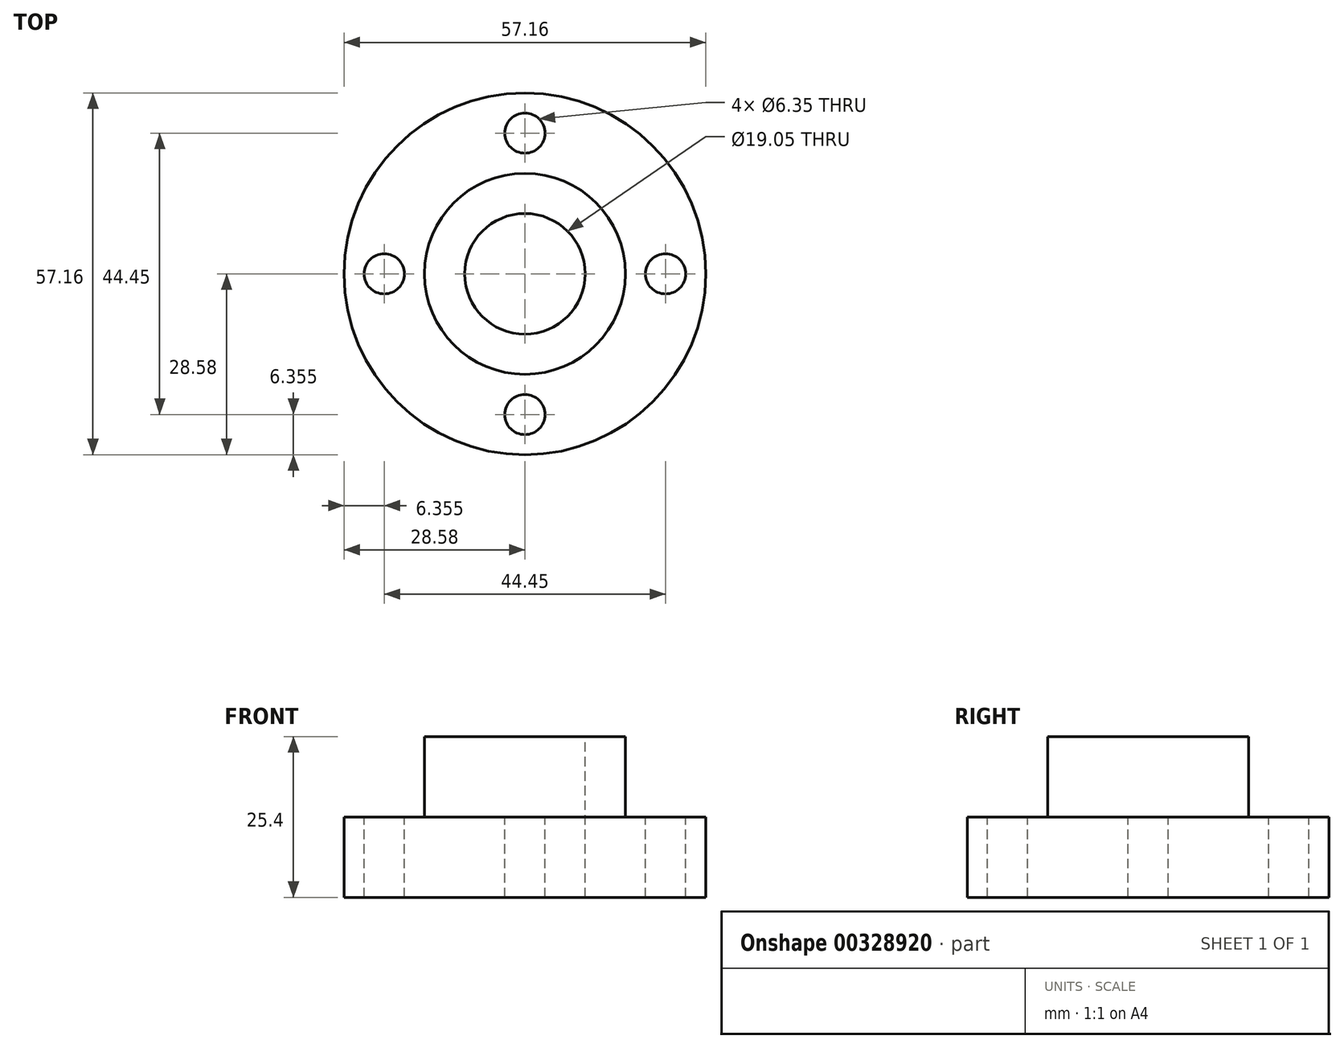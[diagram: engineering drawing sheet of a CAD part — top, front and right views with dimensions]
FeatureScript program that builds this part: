
annotation { "Feature Type Name" : "Feature", "Feature Type Description" : "" }
export const myFeature = defineFeature(function(context is Context, id is Id, definition is map)
    precondition{}
    {
        {
            var Q0;
            Q0=qCreatedBy(makeId("Top.planeOp"),FACE);
            var sketch = newSketch(context, id + "F0", { "sketchPlane" : qUnion([Q0])});
            skCircle(sketch, "E0", {"center": v(0, 0) * mm, "radius": 28.58 * mm});
            skSolve(sketch);
        }
        {
            var Q0;
            Q0=makeQuery(id+"F0.imprint","IMPRINT",FACE,{"disambiguationData":[TD([[makeQuery(id+"F0.imprint","IMPRINT",EDGE,{"derivedFrom":sQuery(id+"F0.wireOp",EDGE,"E0")}),1.0]])]});
            extrude(context, id + "F1", {"entities" : qUnion([Q0]), "depth" : 12.7 * mm});
        }
        {
            var Q0;
            Q0=makeQuery(id+"F1.opExtrude","CAP_FACE",FACE,{"disambiguationData":[OSD([sQuery(id+"F0.wireOp",EDGE,"E0")])],"isStart":false});
            var sketch = newSketch(context, id + "F2", { "sketchPlane" : qUnion([Q0])});
            skCircle(sketch, "E1", {"center": v(0, 0) * mm, "radius": 15.88 * mm});
            skSolve(sketch);
        }
        {
            var Q0;
            Q0=makeQuery(id+"F2.imprint","IMPRINT",FACE,{"disambiguationData":[TD([[makeQuery(id+"F2.imprint","IMPRINT",EDGE,{"derivedFrom":sQuery(id+"F2.wireOp",EDGE,"E1")}),1.0]])]});
            extrude(context, id + "F3", {"entities" : qUnion([Q0]), "operationType" : NewBodyOperationType.ADD, "depth" : 12.7 * mm});
        }
        {
            var Q0;
            Q0=makeQuery(id+"F3.opExtrude","CAP_FACE",FACE,{"disambiguationData":[OSD([sQuery(id+"F2.wireOp",EDGE,"E1")])],"isStart":false});
            var sketch = newSketch(context, id + "F4", { "sketchPlane" : qUnion([Q0])});
            skCircle(sketch, "E2", {"center": v(0, 0) * mm, "radius": 9.53 * mm});
            skSolve(sketch);
        }
        {
            var Q0;
            Q0 = qSketchRegion(id + "F4", true);
            extrude(context, id + "F5", {"entities" : qUnion([Q0]), "operationType" : NewBodyOperationType.REMOVE, "endBound" : BoundingType.THROUGH_ALL, "oppositeDirection" : true, "depth" : 25.4 * mm});
        }
        {
            var Q0;
            Q0=makeQuery(id+"F1.opExtrude","CAP_FACE",FACE,{"disambiguationData":[OSD([sQuery(id+"F0.wireOp",EDGE,"E0")])],"isStart":false});
            var sketch = newSketch(context, id + "F6", { "sketchPlane" : qUnion([Q0])});
            skCircle(sketch, "E3", {"center": v(0, 22.23) * mm, "radius": 3.18 * mm});
            skCircle(sketch, "E4", {"center": v(22.23, 0) * mm, "radius": 3.18 * mm});
            skCircle(sketch, "E5", {"center": v(0, -22.23) * mm, "radius": 3.18 * mm});
            skCircle(sketch, "E6", {"center": v(-22.23, 0) * mm, "radius": 3.18 * mm});
            skSolve(sketch);
        }
        {
            var Q0;
            Q0=makeQuery(id+"F6.imprint","IMPRINT",FACE,{"disambiguationData":[TD([[makeQuery(id+"F6.imprint","IMPRINT",EDGE,{"derivedFrom":sQuery(id+"F6.wireOp",EDGE,"E3")}),1.0]])]});
            var Q1;
            Q1=makeQuery(id+"F6.imprint","IMPRINT",FACE,{"disambiguationData":[TD([[makeQuery(id+"F6.imprint","IMPRINT",EDGE,{"derivedFrom":sQuery(id+"F6.wireOp",EDGE,"E4")}),1.0]])]});
            var Q2;
            Q2=makeQuery(id+"F6.imprint","IMPRINT",FACE,{"disambiguationData":[TD([[makeQuery(id+"F6.imprint","IMPRINT",EDGE,{"derivedFrom":sQuery(id+"F6.wireOp",EDGE,"E6")}),1.0]])]});
            var Q3;
            Q3=makeQuery(id+"F6.imprint","IMPRINT",FACE,{"disambiguationData":[TD([[makeQuery(id+"F6.imprint","IMPRINT",EDGE,{"derivedFrom":sQuery(id+"F6.wireOp",EDGE,"E5")}),1.0]])]});
            extrude(context, id + "F7", {"entities" : qUnion([Q0, Q1, Q2, Q3]), "operationType" : NewBodyOperationType.REMOVE, "endBound" : BoundingType.THROUGH_ALL, "oppositeDirection" : true, "depth" : 25.4 * mm});
        }
    });
